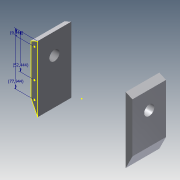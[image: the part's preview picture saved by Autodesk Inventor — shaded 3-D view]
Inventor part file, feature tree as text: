
AUTODESK INVENTOR PART (.ipt)
format: ipt  version: 2013 (Build 170138000, 138)  size: 116,736 bytes
history: native  units: mm
features: sketch x4, hole x2, extrude x1
ambient origin geometry x8: Origin, YZ Plane, XZ Plane, XY Plane, X Axis, Y Axis, Z Axis, Center Point
bodies: Solid1 (feature_tree)
feature tree (7):
  extrude  "Extrusion1"  Depth=73.5mm
  hole  "Hole1"  [1 undecoded]
  hole  "Hole2"  [1 undecoded]
  sketch  "Sketch4"  dims[d16=15.0mm d17=15.0mm d18=6.0mm d19=4.0mm d20=2.0mm d21=90.0deg d22=151.0mm d23=0.0mm d24=5.0mm d25=5.0mm d26=48.0mm d27=5.0mm d28=5.0mm d29=2.0mm d30=6.0mm d31=4.0mm d32=2.0mm d33=90.0deg d34=50.0mm d35=0.0mm d36=9.444444mm d37=52.444444mm d38=77.944444mm]
  sketch  "Sketch1"  dims[d3=10.0mm d4=73.5mm]
  sketch  "Sketch2"  dims[d5=10.0mm d8=10.0mm]
  sketch  "Sketch3"  dims[d9=73.5mm d12=50.0mm d13=0.0mm]
note: 2 required parameter values undecoded (feature->parameter linkage not recoverable at this tier; creation-order binding heuristic only, values carry confidence <= 0.55)
